# Revit family: BE_24624_de_DE
name_source: partatom
category: Lighting Fixtures
revit_build: Autodesk Revit 2017 (Build: 20160225_1515(x64)
units: mm (PartAtom-declared; Revit-internal decimal feet)

## family parameters
Cut with Voids When Loaded = Yes
Host = Face
Light Source = Yes
Part Type = Normal
Room Calculation Point = Yes
Round Connector Dimension = Use Diameter
Shared = No

## types (4) — shared parameters
AC/DC = AC/DC
Aktualisierung = 2021-07-13T04:00:13
Apparent Load = 0 VA
BEGA_Dummy = No
BEGA_IES = Yes
BEGA_Intern = Yes
BEGA_Intern_Konstruktion = Yes
BEGA_Intern_an = Yes
BEGA_Intern_aus = Yes
Befestigungsabstand = 160 mm
Befestigungsbohrung = Ø 4,3 mm
Beschreibung_Sonderanfertigung = Hier können Sie Informationen zur Sonderanfertigung eintragen.
CE_Konformität = ja
Color Filter = 16777215
Description = Deckenaufbau-Tiefstrahler
Dimming Lamp Color Temperature Shift = <None>
Energieeffizienzklasse = LED A++ - A
Farbwiedergabeindex = CRI > 80
Frequenz = 0/50-60 Hz
Gewicht = 2.65 kg
Lamp = LED 17.2 W
Lastklassifizierung = Beleuchtung
Lebensdauerkriterien = L70B50 @ 25 °C = 200000 h
M_A = No
Manufacturer = BEGA
Material_03 = BEGA_Oberfläche_Weiss_matt
Material_06 = BEGA_Oberfläche_Edelstahl_gebürstet
Material_09 = BEGA_Glas_klar
Material_13 = BEGA_Kunststoff_matt
Material_15 = BEGA_Leuchtmedium_matt
Material_17 = BEGA_Reflektor
Material_18 = BEGA_Gummi_schwarz
Produktdatenblatt = http://www.bega.de
Schutzart = IP 65
Schutzklasse = I
Sonderanfertigung = No
Spannung = 240 V
Tilt Angle = 0.00°
URL = https://www.bega.com
Umgebungstemperatur = 25 °C
zero-valued in all types: Default Elevation

## per-type parameters (varying)
| type | Bestellnummer | Farbtemperatur | LED_Modulbezeichnung | Lampenlichtstrom | Leuchtenlichtstrom | Logo | M_G | M_W | Model | Photometric Web File |
| BEGA_24624_Weiß_K4 | 24624WK4 | 4000 K | LED-0785/840 | 3180 lm | 2262 lm | <None> | No | Yes | 24624WK4 | BE_24624K4.IES |
| BEGA_24624_Grafit_K4 | 24624K4 | 4000 K | LED-0785/840 | 3180 lm | 2262 lm | BEGA_Logo.png | Yes | No | 24624K4 | BE_24624K4.IES |
| BEGA_24624_Weiß_K3 | 24624WK3 | 3000 K | LED-0785/830 | 3100 lm | 2205 lm | BEGA_Logo.png | No | Yes | 24624WK3 | BE_24624K3.IES |
| BEGA_24624_Grafit_K3 | 24624K3 | 3000 K | LED-0785/830 | 3100 lm | 2205 lm | BEGA_Logo.png | Yes | No | 24624K3 | BE_24624K3.IES |
